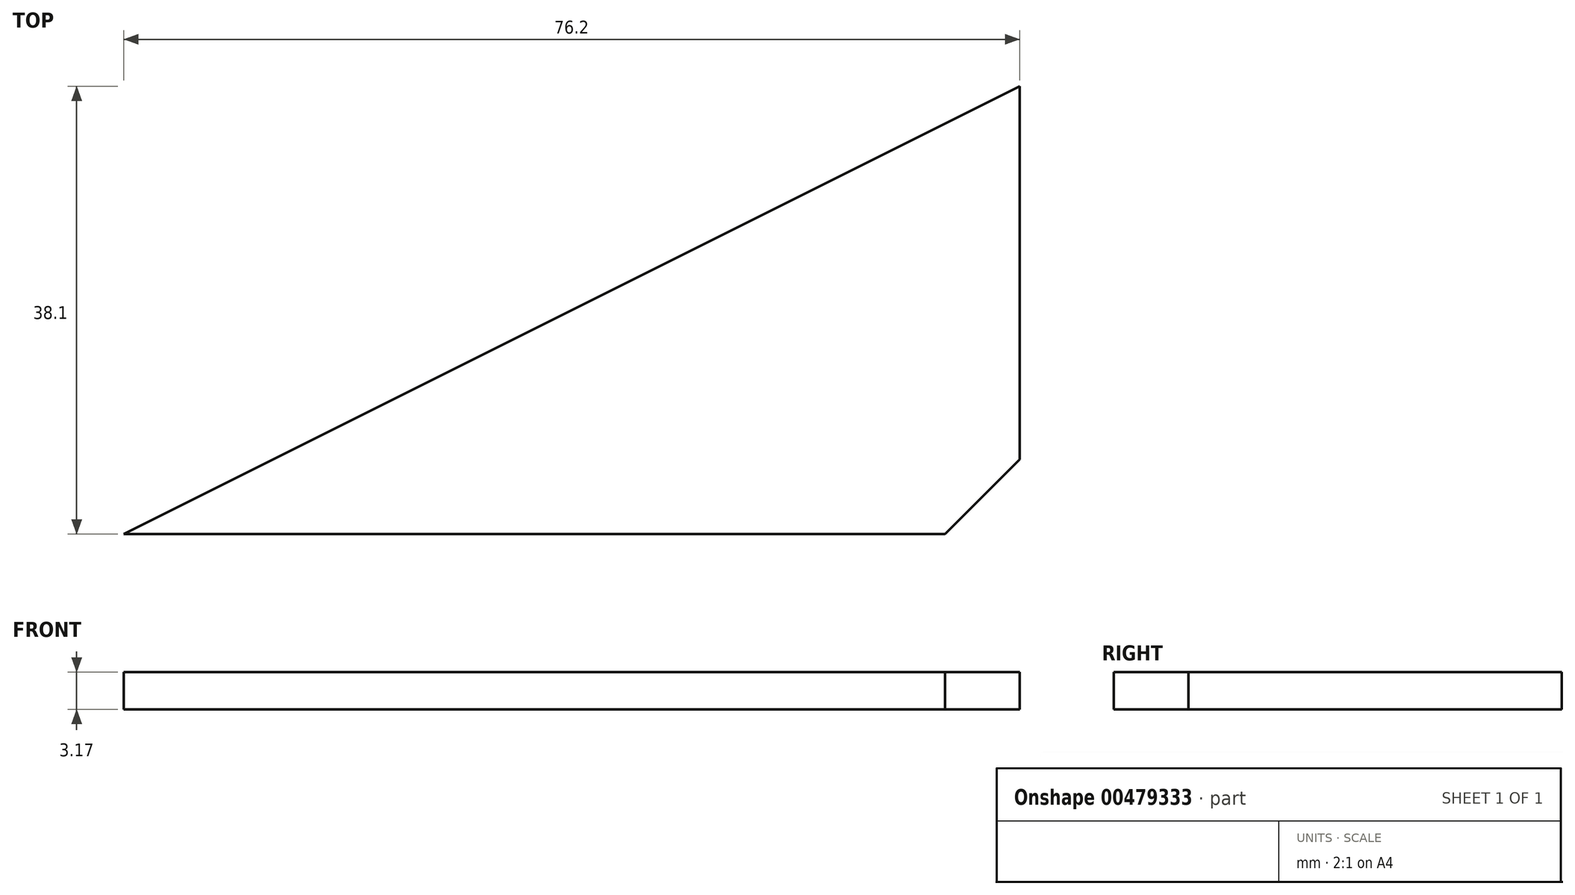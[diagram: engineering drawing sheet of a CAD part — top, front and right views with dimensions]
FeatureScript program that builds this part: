
annotation { "Feature Type Name" : "Feature", "Feature Type Description" : "" }
export const myFeature = defineFeature(function(context is Context, id is Id, definition is map)
    precondition{}
    {
        {
            var Q0;
            Q0=qCreatedBy(makeId("Top.planeOp"),FACE);
            var sketch = newSketch(context, id + "F0", { "sketchPlane" : qUnion([Q0])});
            skLineSegment(sketch, "E0.top", {"start": v(0, -38.1) * mm, "end": v(76.2, -38.1) * mm});
            skLineSegment(sketch, "E0.right", {"start": v(76.2, 0) * mm, "end": v(76.2, -38.1) * mm});
            skLineSegment(sketch, "E1", {"start": v(76.2, 0) * mm, "end": v(0, -38.1) * mm});
            skSolve(sketch);
        }
        {
            var Q0;
            Q0=makeQuery(id+"F0.imprint","IMPRINT",FACE,{"disambiguationData":[TD([[makeQuery(id+"F0.imprint","IMPRINT",EDGE,{"derivedFrom":sQuery(id+"F0.wireOp",EDGE,"E0.top")}),1.0]])]});
            extrude(context, id + "F1", {"entities" : qUnion([Q0]), "depth" : 3.17 * mm});
        }
        {
            var Q0;
            Q0=makeQuery(id+"F1.opExtrude","SWEPT_EDGE",EDGE,{"disambiguationData":[OSD([sQuery(id+"F0.wireOp",EDGE,"E0.top"),sQuery(id+"F0.wireOp",EDGE,"E0.right")])]});
            chamfer(context, id + "F2", {"entities" : qUnion([Q0]), "width" : 6.35 * mm, "tangentPropagation" : true});
        }
    });
